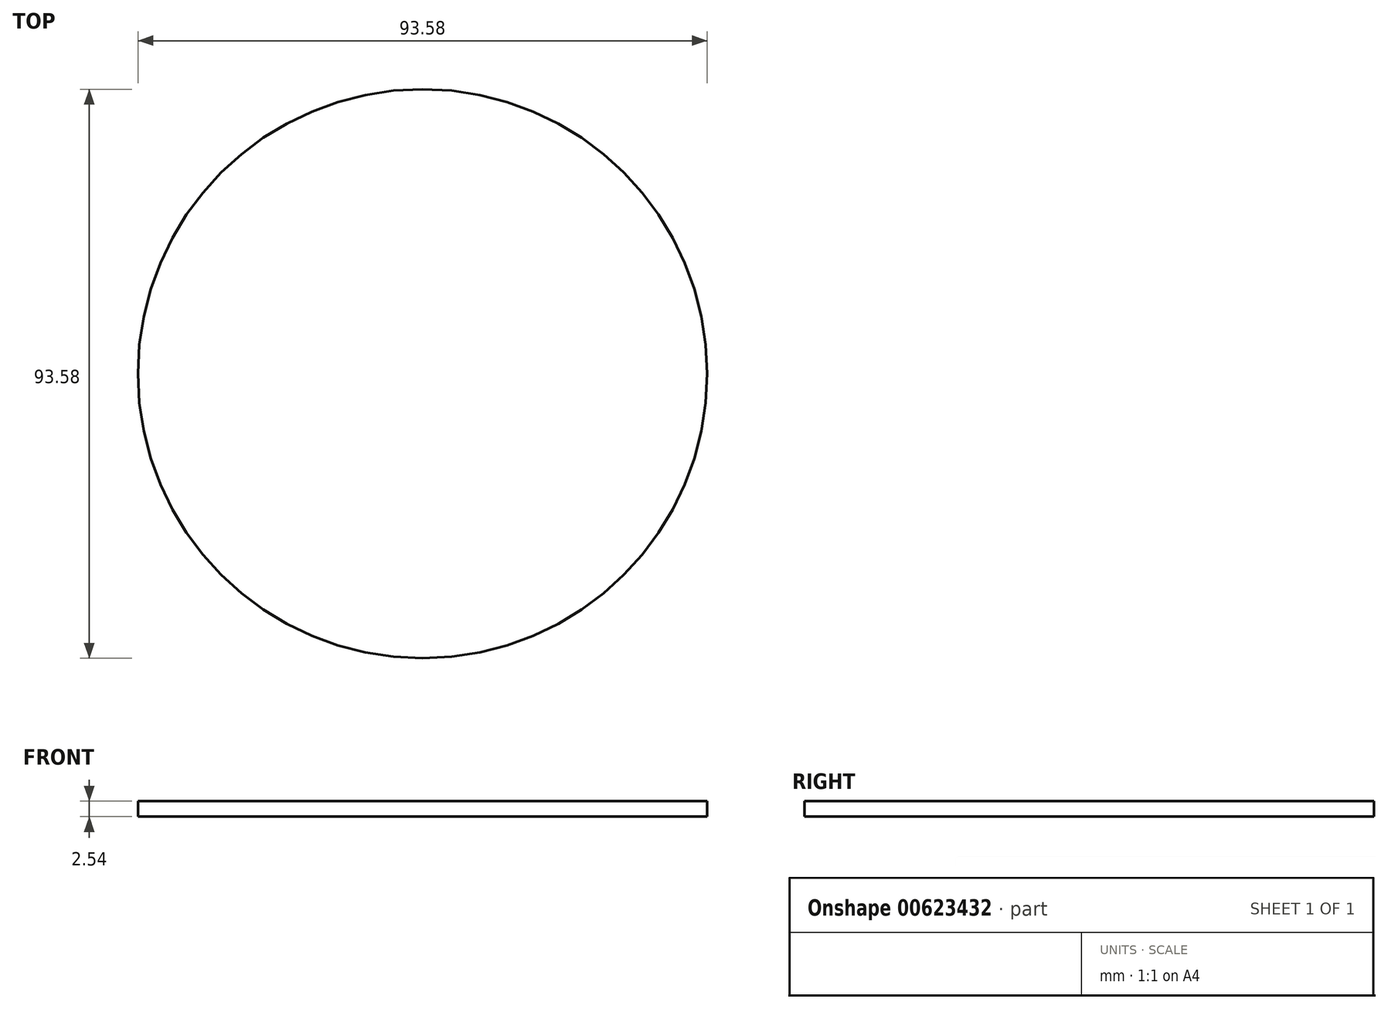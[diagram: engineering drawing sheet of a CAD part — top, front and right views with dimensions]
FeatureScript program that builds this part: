
annotation { "Feature Type Name" : "Feature", "Feature Type Description" : "" }
export const myFeature = defineFeature(function(context is Context, id is Id, definition is map)
    precondition{}
    {
        {
            var Q0;
            Q0=qCreatedBy(makeId("Top.planeOp"),FACE);
            var sketch = newSketch(context, id + "F0", { "sketchPlane" : qUnion([Q0])});
            skCircle(sketch, "E0", {"center": v(0, 0) * mm, "radius": 46.79 * mm});
            skSolve(sketch);
        }
        {
            var Q0;
            Q0=makeQuery(id+"F0.imprint","IMPRINT",FACE,{"disambiguationData":[TD([[makeQuery(id+"F0.imprint","IMPRINT",EDGE,{"derivedFrom":sQuery(id+"F0.wireOp",EDGE,"E0")}),1.0]])]});
            extrude(context, id + "F1", {"entities" : qUnion([Q0]), "depth" : 2.54 * mm, "offsetDistance" : 25.4 * mm});
        }
    });
